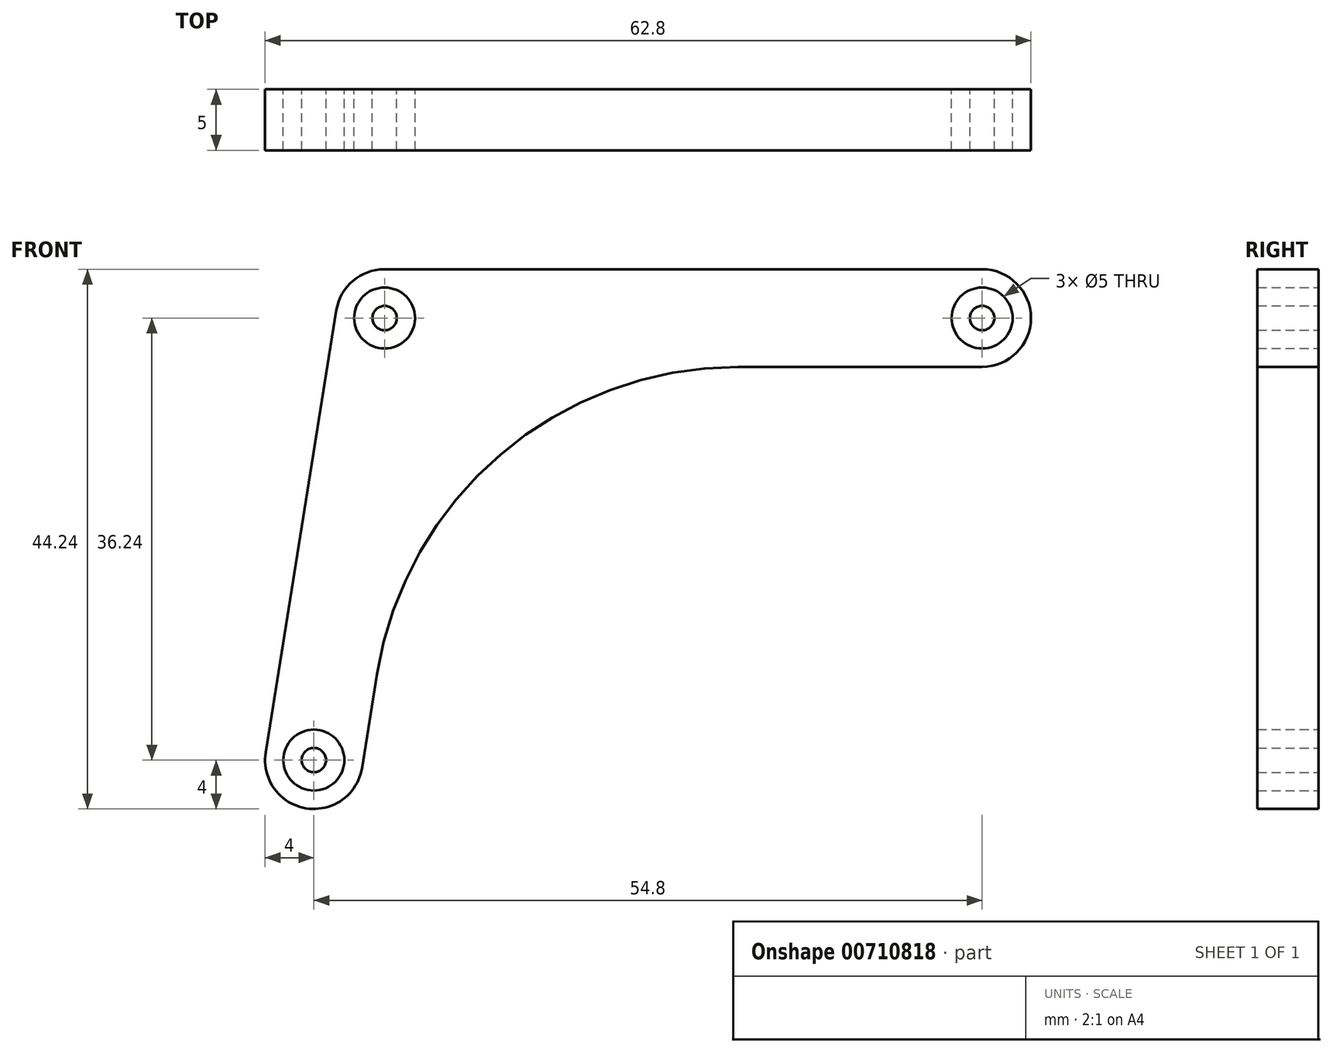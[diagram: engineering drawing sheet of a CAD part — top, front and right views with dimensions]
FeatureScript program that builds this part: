
annotation { "Feature Type Name" : "Feature", "Feature Type Description" : "" }
export const myFeature = defineFeature(function(context is Context, id is Id, definition is map)
    precondition{}
    {
        {
            var Q0;
            Q0=qCreatedBy(makeId("Front.planeOp"),FACE);
            var sketch = newSketch(context, id + "F0", { "sketchPlane" : qUnion([Q0])});
            skCircle(sketch, "E0", {"center": v(0, 0) * mm, "radius": 2.5 * mm});
            skCircle(sketch, "E1", {"center": v(-5.8, -36.24) * mm, "radius": 2.5 * mm});
            skCircle(sketch, "E2", {"center": v(49, 0) * mm, "radius": 2.5 * mm});
            skArc(sketch, "E3", {"start": v(0, 4) * mm, "mid": v(-2.6, 3.04) * mm, "end": v(-3.95, 0.63) * mm});
            skArc(sketch, "E4", {"start": v(-9.75, -35.6) * mm, "mid": v(-6.43, -40.19) * mm, "end": v(-1.85, -36.87) * mm});
            skArc(sketch, "E5", {"start": v(49, -4) * mm, "mid": v(53, 0) * mm, "end": v(49, 4) * mm});
            skLineSegment(sketch, "E6", {"start": v(-3.95, 0.63) * mm, "end": v(-9.75, -35.6) * mm});
            skLineSegment(sketch, "E7", {"start": v(0, 4) * mm, "end": v(49, 4) * mm});
            skLineSegment(sketch, "E8", {"start": v(-0.63, -29.26) * mm, "end": v(-1.85, -36.87) * mm});
            skLineSegment(sketch, "E9", {"start": v(29, -4) * mm, "end": v(49, -4) * mm});
            skPoint(sketch, "E10.visualSharp", {"position": v(3.41, -4) * mm});
            skArc(sketch, "E10.filletArc", {"start": v(29, -4) * mm, "mid": v(9.53, -11.17) * mm, "end": v(-0.63, -29.26) * mm});
            skSolve(sketch);
        }
        {
            var Q0;
            Q0=makeQuery(id+"F0.imprint","IMPRINT",FACE,{"disambiguationData":[TD([[makeQuery(id+"F0.imprint","IMPRINT",EDGE,{"derivedFrom":sQuery(id+"F0.wireOp",EDGE,"E0")}),-1.0]])]});
            extrude(context, id + "F1", {"entities" : qUnion([Q0]), "depth" : 5 * mm, "offsetDistance" : 25 * mm});
        }
        {
            var Q0;
            Q0=qCreatedBy(makeId("Front.planeOp"),FACE);
            var sketch = newSketch(context, id + "F2", { "sketchPlane" : qUnion([Q0])});
            skCircle(sketch, "E11", {"center": v(0, 0) * mm, "radius": 1 * mm});
            skCircle(sketch, "E12.0", {"center": v(-5.8, -36.24) * mm, "radius": 2.5 * mm});
            skCircle(sketch, "E12.1", {"center": v(49, 0) * mm, "radius": 2.5 * mm});
            skCircle(sketch, "E13", {"center": v(-5.8, -36.24) * mm, "radius": 1 * mm});
            skCircle(sketch, "E14", {"center": v(49, 0) * mm, "radius": 1 * mm});
            skSolve(sketch);
        }
        {
            var Q0;
            Q0=makeQuery(id+"F2.imprint","IMPRINT",FACE,{"disambiguationData":[TD([[makeQuery(id+"F2.imprint","IMPRINT",EDGE,{"derivedFrom":sQuery(id+"F2.wireOp",EDGE,"E11")}),1.0]])]});
            var Q1;
            Q1=makeQuery(id+"F2.imprint","IMPRINT",FACE,{"disambiguationData":[TD([[makeQuery(id+"F2.imprint","IMPRINT",EDGE,{"derivedFrom":sQuery(id+"F2.wireOp",EDGE,"E14")}),1.0]])]});
            var Q2;
            Q2=makeQuery(id+"F2.imprint","IMPRINT",FACE,{"disambiguationData":[TD([[makeQuery(id+"F2.imprint","IMPRINT",EDGE,{"derivedFrom":sQuery(id+"F2.wireOp",EDGE,"E13")}),1.0]])]});
            extrude(context, id + "F3", {"entities" : qUnion([Q0, Q1, Q2]), "depth" : 5 * mm, "offsetDistance" : 25 * mm});
        }
    });
